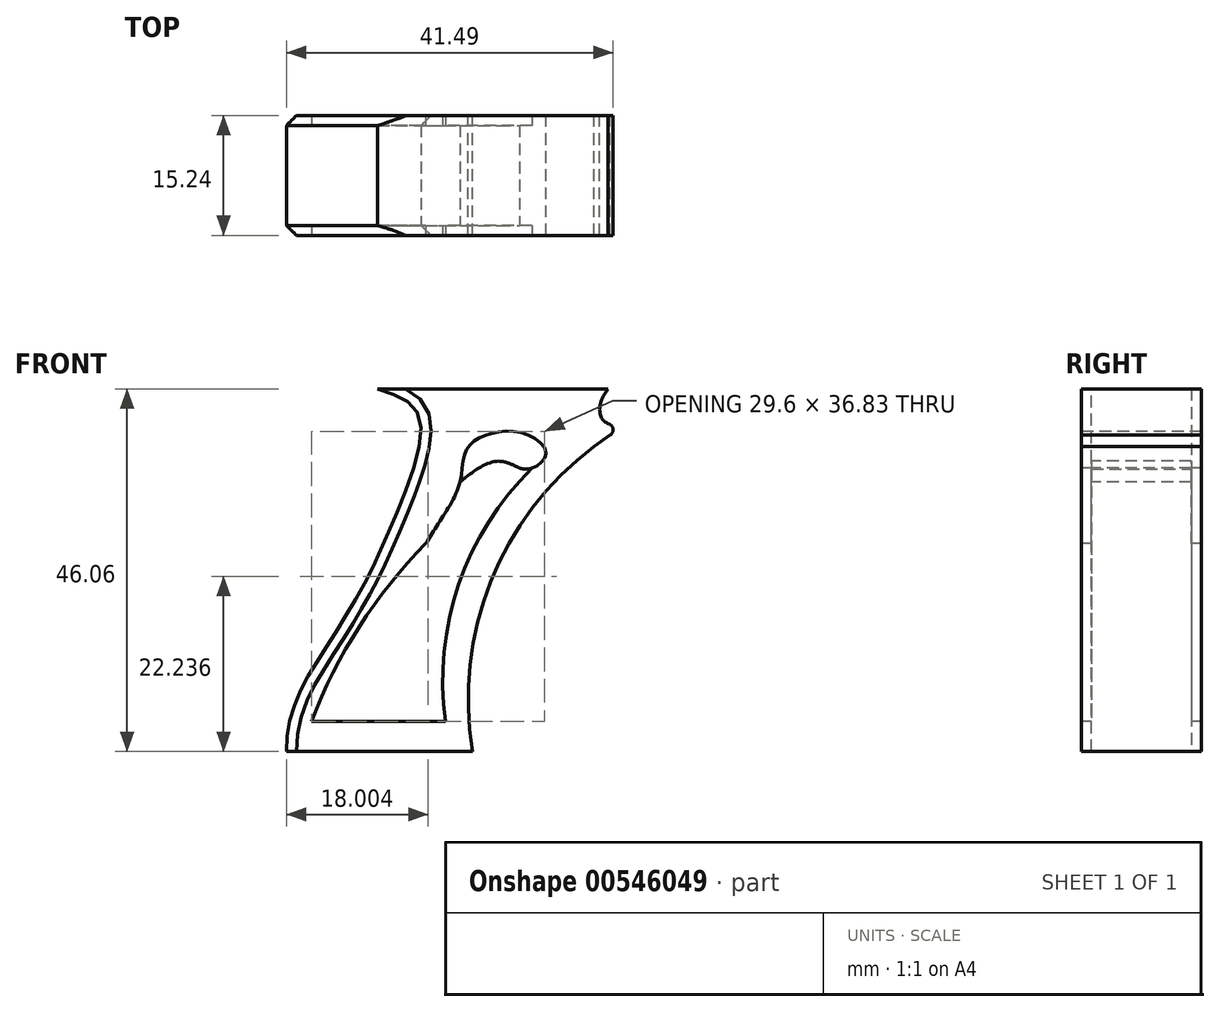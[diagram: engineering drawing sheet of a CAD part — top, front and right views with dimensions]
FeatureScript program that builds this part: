
annotation { "Feature Type Name" : "Feature", "Feature Type Description" : "" }
export const myFeature = defineFeature(function(context is Context, id is Id, definition is map)
    precondition{}
    {
        {
            var Q0;
            Q0=qCreatedBy(makeId("Front.planeOp"),FACE);
            var sketch = newSketch(context, id + "F0", { "sketchPlane" : qUnion([Q0])});
            skLineSegment(sketch, "E0", {"start": v(0, 50.83) * mm, "end": v(16.35, 50.8) * mm});
            skLineSegment(sketch, "E1", {"start": v(0, 50.83) * mm, "end": v(25.4, 50.81) * mm});
            skPoint(sketch, "E1.endSnap0", {"position": v(8.17, 50.81) * mm});
            skFitSpline(sketch, "E2", {"points": [v(25.4, 50.81) * mm, v(24.58, 49.34) * mm, v(24.48, 47.43) * mm, v(25.4, 46.43) * mm, v(26.69, 46.13) * mm, v(27.43, 46.07) * mm], "startDerivative": vector(-4.23, -6.07) * mm, "endDerivative": vector(4.44, -0.67) * mm});
            skPoint(sketch, "E3.start.orphan", {"position": v(21.91, 23.05) * mm});
            skPoint(sketch, "E4.end.orphan", {"position": v(16.39, 0.04) * mm});
            skLineSegment(sketch, "E5", {"start": v(0, 0) * mm, "end": v(9.35, 0) * mm});
            skArc(sketch, "E6", {"start": v(27.43, 46.07) * mm, "mid": v(26.56, 45.54) * mm, "end": v(25.7, 44.99) * mm});
            skLineSegment(sketch, "E7", {"start": v(0, 50.83) * mm, "end": v(-3.84, 50.83) * mm});
            skFitSpline(sketch, "E8", {"points": [v(-14.13, 0) * mm, v(-15.4, 4.77) * mm, v(-14.13, 11.4) * mm, v(-10.4, 17.94) * mm, v(-5.54, 26.12) * mm, v(-1.16, 35.71) * mm, v(1.4, 47.43) * mm, v(-3.84, 50.83) * mm], "startDerivative": vector(-15.36, 39.94) * mm, "endDerivative": vector(-53.81, 17.34) * mm});
            skPoint(sketch, "E9.orphan", {"position": v(10.45, 26.15) * mm});
            skLineSegment(sketch, "E10", {"start": v(-15.4, 4.77) * mm, "end": v(8.24, 4.77) * mm});
            skArc(sketch, "E11", {"start": v(44.19, 50.81) * mm, "mid": v(37.08, 41.12) * mm, "end": v(25.7, 44.99) * mm});
            skLineSegment(sketch, "E12", {"start": v(34.03, 50.81) * mm, "end": v(44.19, 50.81) * mm});
            skArc(sketch, "E13", {"start": v(36.23, 38.3) * mm, "mid": v(29.17, 39.08) * mm, "end": v(23.63, 43.52) * mm});
            skArc(sketch, "E14.trimOffspring", {"start": v(23.63, 43.52) * mm, "mid": v(9.67, 24) * mm, "end": v(9.35, 0) * mm});
            skLineSegment(sketch, "E15", {"start": v(23.63, 43.52) * mm, "end": v(25.7, 44.99) * mm});
            skSolve(sketch);
        }
        {
            var Q0;
            {var subQ0=sQuery(id+"F0.wireOp",EDGE,"X7WkOkcv-S1le-CiY6-r1zo-8j0lH5rAS3uE");Q0=makeQuery(id+"F0.imprint","IMPRINT",FACE,{"disambiguationData":[TD([[makeQuery(id+"F0.imprint","IMPRINT",EDGE,{"derivedFrom":subQ0}),1.0]])]});}
            var Q1;
            {var subQ0=sQuery(id+"F0.wireOp",EDGE,"E7");Q1=makeQuery(id+"F0.imprint","IMPRINT",FACE,{"disambiguationData":[TD([[makeQuery(id+"F0.imprint","IMPRINT",EDGE,{"derivedFrom":subQ0}),1.0]])]});}
            var Q2;
            Q2=makeQuery(id+"F0.imprint","IMPRINT",FACE,{"disambiguationData":[TD([[makeQuery(id+"F0.imprint","IMPRINT",EDGE,{"derivedFrom":sQuery(id+"F0.wireOp",EDGE,"E1")}),-1.0]])]});
            extrude(context, id + "F1", {"entities" : qUnion([Q0, Q1, Q2]), "depth" : 15.24 * mm, "offsetDistance" : 25.4 * mm});
        }
        {
            var Q0;
            Q0=makeQuery(id+"F1.opExtrude","CAP_FACE",FACE,{"disambiguationData":[OSD([sQuery(id+"F0.wireOp",EDGE,"E1"),sQuery(id+"F0.wireOp",EDGE,"E2"),sQuery(id+"F0.wireOp",EDGE,"E6"),sQuery(id+"F0.wireOp",EDGE,"E7"),sQuery(id+"F0.wireOp",EDGE,"E8"),sQuery(id+"F0.wireOp",EDGE,"E10")])],"isStart":false});
            var sketch = newSketch(context, id + "F2", { "sketchPlane" : qUnion([Q0])});
            skLineSegment(sketch, "E16", {"start": v(-12.21, 8.59) * mm, "end": v(4.77, 8.59) * mm});
            skArc(sketch, "E17", {"start": v(15.77, 40.76) * mm, "mid": v(6.46, 25.98) * mm, "end": v(4.77, 8.59) * mm});
            skArc(sketch, "E18", {"start": v(2.27, 31.2) * mm, "mid": v(-6.15, 20.65) * mm, "end": v(-12.21, 8.59) * mm});
            skFitSpline(sketch, "E19", {"points": [v(2.27, 31.2) * mm, v(4.5, 34.7) * mm, v(6.62, 39.03) * mm, v(7.42, 43.05) * mm, v(9.93, 44.96) * mm, v(14.76, 45.16) * mm, v(17.58, 42.65) * mm, v(15.77, 40.76) * mm, v(14.22, 40.76) * mm], "startDerivative": vector(15.75, 25.38) * mm, "endDerivative": vector(-17.2, 3.75) * mm});
            skFitSpline(sketch, "E20", {"points": [v(6.62, 39.03) * mm, v(7.92, 40.03) * mm, v(11.54, 41.64) * mm, v(14.22, 40.76) * mm, v(14.7, 40.66) * mm], "startDerivative": vector(4.81, 3.87) * mm, "endDerivative": vector(3.13, -0.2) * mm});
            skFitSpline(sketch, "E21", {"points": [v(15.77, 40.76) * mm, v(15.77, 42.15) * mm, v(13.86, 42.15) * mm, v(11.54, 41.64) * mm, v(9.53, 39.32) * mm], "startDerivative": vector(1.92, 8.55) * mm, "endDerivative": vector(-6.24, -9.41) * mm});
            skSolve(sketch);
        }
        {
            var Q0;
            Q0 = qSketchRegion(id + "F2", true);
            extrude(context, id + "F3", {"entities" : qUnion([Q0]), "operationType" : NewBodyOperationType.REMOVE, "oppositeDirection" : true, "depth" : 15.24 * mm, "offsetDistance" : 25.4 * mm});
        }
        {
            var Q0;
            Q0=makeQuery(id+"F2.imprint","IMPRINT",FACE,{"disambiguationData":[TD([[makeQuery(id+"F2.imprint","IMPRINT",EDGE,{"derivedFrom":sQuery(id+"F2.wireOp",EDGE,"E16")}),1.0]])]});
            extrude(context, id + "F4", {"entities" : qUnion([Q0]), "operationType" : NewBodyOperationType.ADD, "oppositeDirection" : true, "depth" : 13.97 * mm, "offsetDistance" : 25.4 * mm});
        }
        {
            var Q0;
            Q0=makeQuery(id+"F2.imprint","IMPRINT",FACE,{"disambiguationData":[TD([[makeQuery(id+"F2.imprint","IMPRINT",EDGE,{"derivedFrom":sQuery(id+"F2.wireOp",EDGE,"E16")}),1.0]])]});
            extrude(context, id + "F5", {"entities" : qUnion([Q0]), "operationType" : NewBodyOperationType.REMOVE, "oppositeDirection" : true, "depth" : 1.27 * mm, "offsetDistance" : 25.4 * mm});
        }
        {
            var Q0;
            Q0=makeQuery(id+"F1.opExtrude","CAP_EDGE",EDGE,{"disambiguationData":[OSD([sQuery(id+"F0.wireOp",EDGE,"E8")])],"isStart":false});
            var Q1;
            Q1=makeQuery(id+"F1.opExtrude","CAP_EDGE",EDGE,{"disambiguationData":[OSD([sQuery(id+"F0.wireOp",EDGE,"E8")])],"isStart":true});
            chamfer(context, id + "F6", {"entities" : qUnion([Q0, Q1]), "width" : 1.27 * mm, "tangentPropagation" : true});
        }
        {
            var Q0;
            Q0=makeQuery(id+"F1.opExtrude","SWEPT_EDGE",EDGE,{"disambiguationData":[OSD([sQuery(id+"F0.wireOp",EDGE,"E2"),sQuery(id+"F0.wireOp",EDGE,"E6")])]});
            fillet(context, id + "F7", {"entities" : qUnion([Q0]), "radius" : 0.76 * mm, "tangentPropagation" : true, "allowEdgeOverflow" : false});
        }
    });
